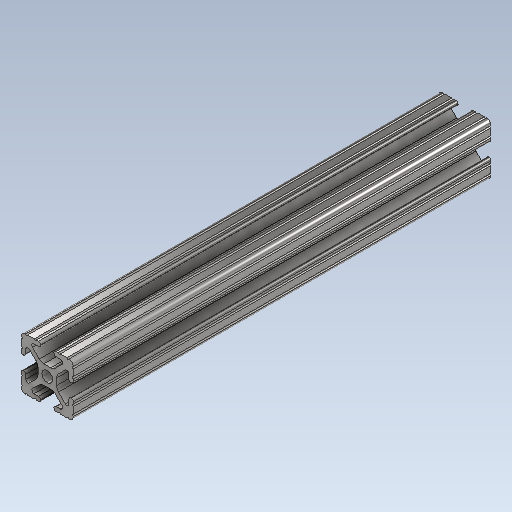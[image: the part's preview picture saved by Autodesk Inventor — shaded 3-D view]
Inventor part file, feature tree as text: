
AUTODESK INVENTOR PART (.ipt)
format: ipt  version: 2020 (Build 240168000, 168)  size: 287,232 bytes
history: native  units: in
note: dims shown in document units (in); Inventor stores cm internally (conversion verified against a paired STEP export)
features: extrude x1, sketch x1
ambient origin geometry x8: Origin, YZ Plane, XZ Plane, XY Plane, X Axis, Y Axis, Z Axis, Center Point
bodies: Solid1 (feature_tree)
feature tree (2):
  extrude  "Extrusion1"  [1 undecoded]
  sketch  "Sketch1"  dims[d0=8.0in d1=0.0in]
note: 1 required parameter value undecoded (feature->parameter linkage not recoverable at this tier; creation-order binding heuristic only, values carry confidence <= 0.55)
